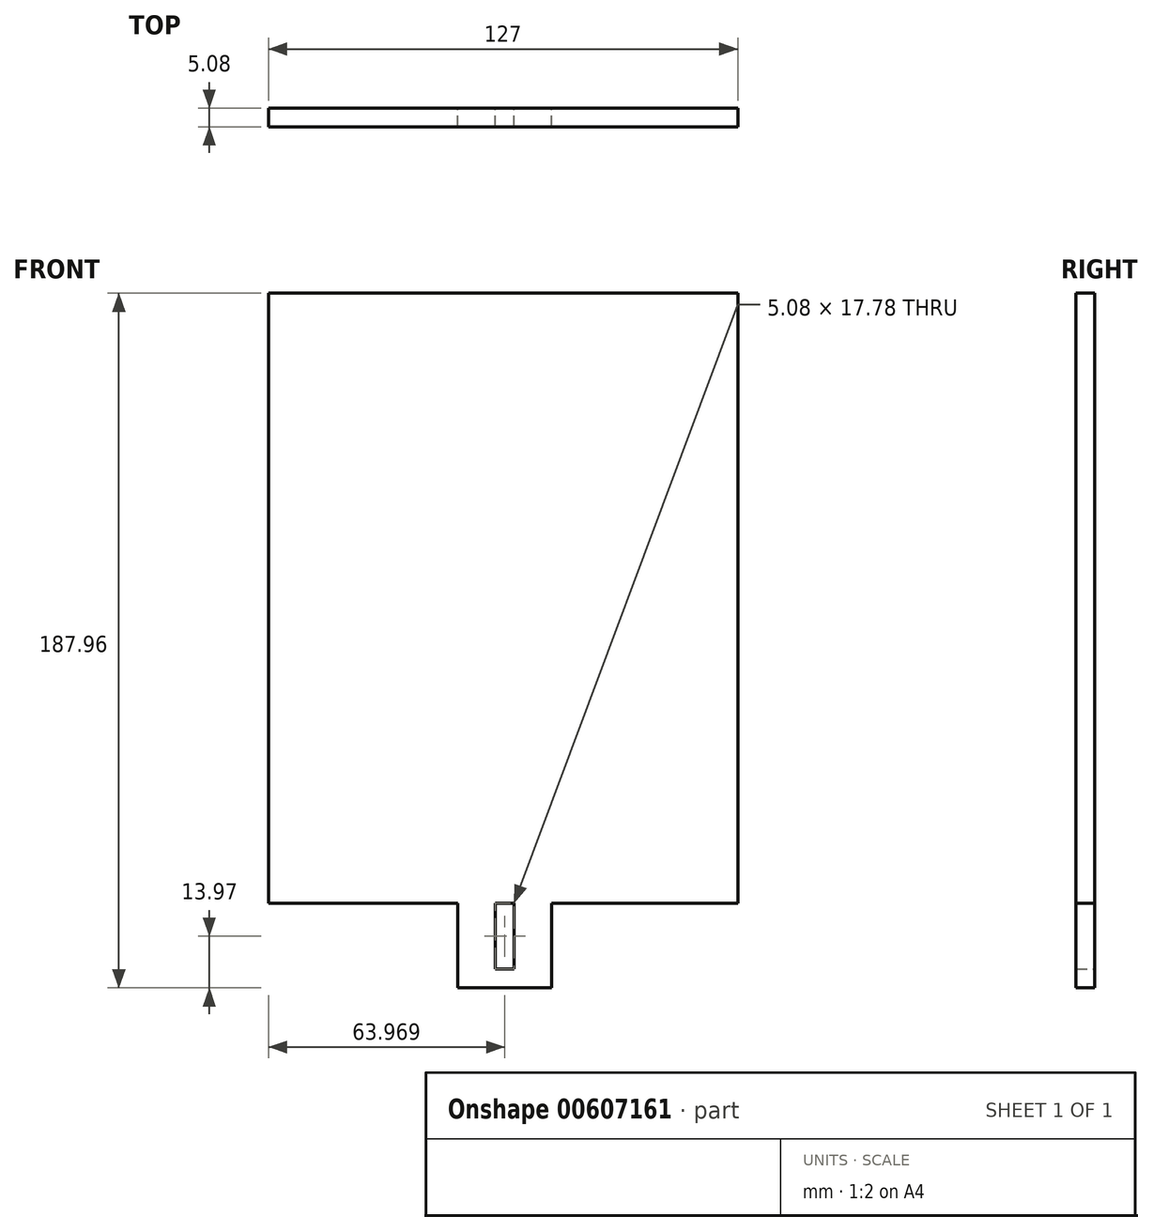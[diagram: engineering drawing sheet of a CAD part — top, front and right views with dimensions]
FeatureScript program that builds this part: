
annotation { "Feature Type Name" : "Feature", "Feature Type Description" : "" }
export const myFeature = defineFeature(function(context is Context, id is Id, definition is map)
    precondition{}
    {
        {
            var Q0;
            Q0=qCreatedBy(makeId("Front.planeOp"),FACE);
            var sketch = newSketch(context, id + "F0", { "sketchPlane" : qUnion([Q0])});
            skLineSegment(sketch, "E0.bottom", {"start": v(63.5, 82.55) * mm, "end": v(-63.5, 82.55) * mm});
            skLineSegment(sketch, "E0.top", {"start": v(63.5, -82.55) * mm, "end": v(-63.5, -82.55) * mm});
            skLineSegment(sketch, "E0.left", {"start": v(63.5, 82.55) * mm, "end": v(63.5, -82.55) * mm});
            skLineSegment(sketch, "E0.right", {"start": v(-63.5, 82.55) * mm, "end": v(-63.5, -82.55) * mm});
            skPoint(sketch, "E0.middle", {"position": v(0, 0) * mm});
            skLineSegment(sketch, "E1", {"start": v(-12.23, -82.55) * mm, "end": v(-12.23, -105.4) * mm});
            skLineSegment(sketch, "E2", {"start": v(-12.23, -105.4) * mm, "end": v(13.17, -105.4) * mm});
            skLineSegment(sketch, "E3", {"start": v(13.17, -105.4) * mm, "end": v(13.17, -82.55) * mm});
            skLineSegment(sketch, "E4", {"start": v(-12.23, -119.9) * mm, "end": v(-2.07, -119.9) * mm});
            skLineSegment(sketch, "E5", {"start": v(-2.07, -82.55) * mm, "end": v(-2.07, -100.33) * mm});
            skLineSegment(sketch, "E6", {"start": v(-2.07, -100.33) * mm, "end": v(3, -100.33) * mm});
            skLineSegment(sketch, "E7", {"start": v(3, -100.33) * mm, "end": v(3, -82.55) * mm});
            skSolve(sketch);
        }
        {
            var Q0;
            Q0 = qSketchRegion(id + "F0", true);
            extrude(context, id + "F1", {"entities" : qUnion([Q0]), "depth" : 5.08 * mm, "offsetDistance" : 25.4 * mm});
        }
    });
